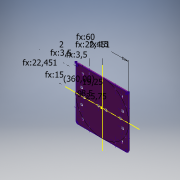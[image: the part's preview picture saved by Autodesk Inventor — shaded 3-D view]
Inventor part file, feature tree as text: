
AUTODESK INVENTOR PART (.ipt)
format: ipt  version: 2019 (Build 230136000, 136)  size: 169,984 bytes
history: native  units: mm
features: hole x4, other x1, sketch x1, extrude x1
ambient origin geometry x8: Origin, YZ Plane, XZ Plane, XY Plane, X Axis, Y Axis, Z Axis, Center Point
bodies: Solid1 (feature_tree)
feature tree (7):
  other  "<userpath>\OneDrive - Van Ierland\Documents\Inventor\FlightSim\Instrument.xlsx"
  sketch  "Sketch1"  dims[d0=60.0mm d1=2.0mm d2=22.45064mm d3=22.45064mm d4=15.0mm d5=15.0mm d6=3.5mm d7=3.5mm d8=40.0mm d10=360.0deg d12=1.5mm d13=0.0mm d14=3.4mm d15=6.0mm d16=6.3mm d17=2.0mm d18=90.0deg d19=8.0mm d20=20.594885mm d21=2.4mm d22=6.0mm d23=4.4mm d24=2.0mm d25=90.0deg d26=8.0mm d27=20.594885mm d28=9.0mm d29=3.0mm d30=6.0mm d31=4.0mm d32=2.0mm d33=90.0deg d34=8.0mm d35=20.594885mm d36=25.75mm d37=3.0mm d38=6.0mm d39=4.0mm d40=2.0mm d41=90.0deg d42=8.0mm d43=20.594885mm d44=0.0mm d45=0.0mm d46=0.0mm d47=0.0mm d48=19.25mm d49=8.5mm]
  extrude  "Extrusion1"  Depth=2.0mm
  hole  "Hole1"  [1 undecoded]
  hole  "Hole2"  [1 undecoded]
  hole  "Hole3"  [1 undecoded]
  hole  "Hole4"  [1 undecoded]
note: 4 required parameter values undecoded (feature->parameter linkage not recoverable at this tier; creation-order binding heuristic only, values carry confidence <= 0.55)
